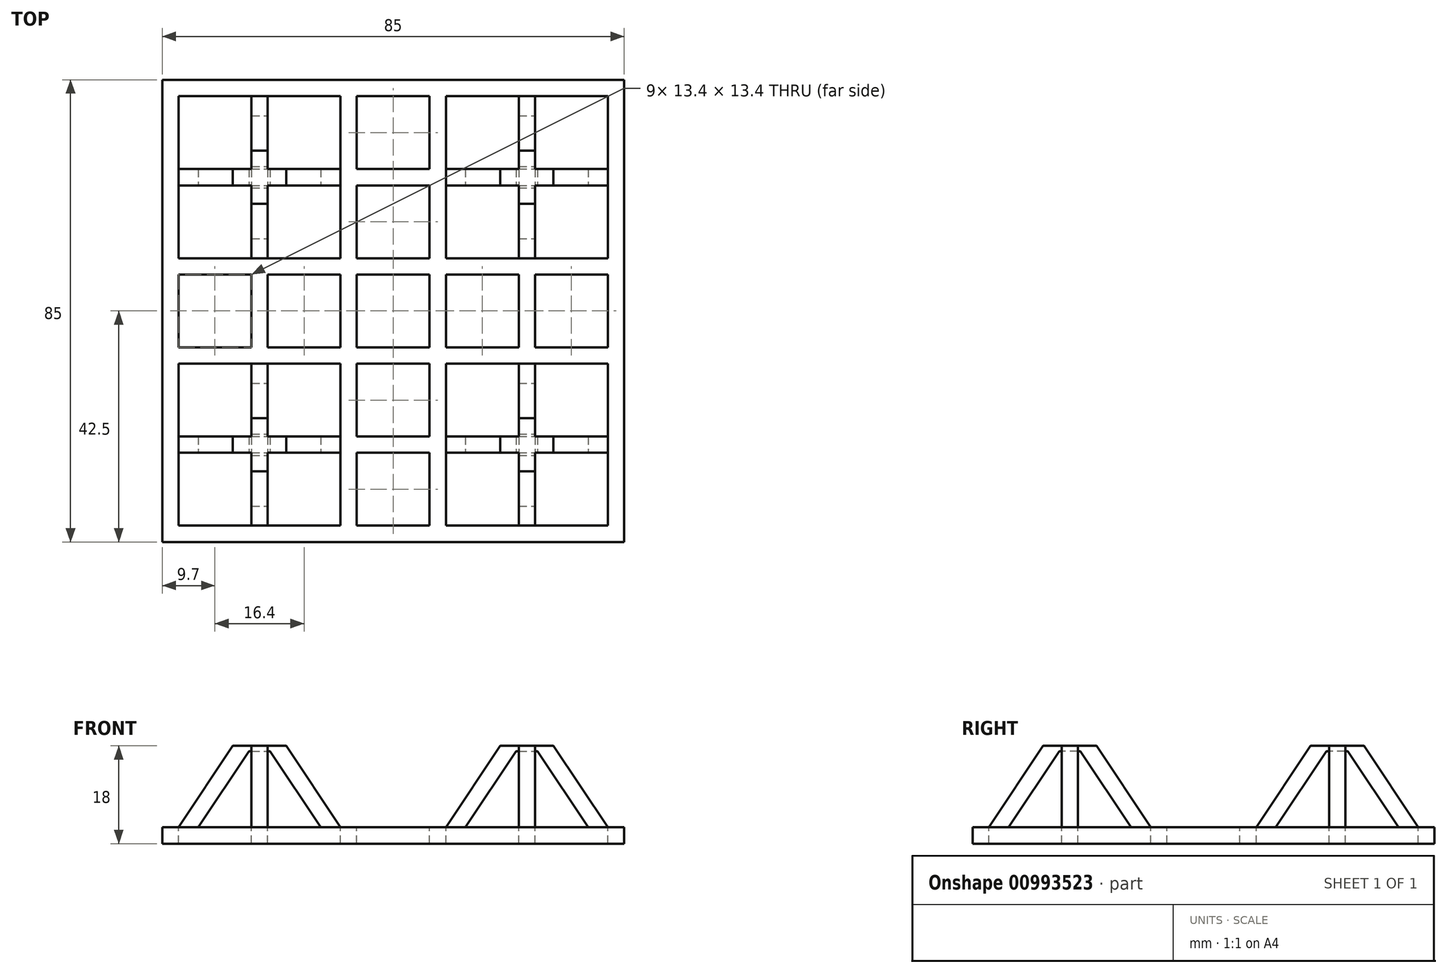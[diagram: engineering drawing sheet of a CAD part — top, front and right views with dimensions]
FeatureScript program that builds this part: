
annotation { "Feature Type Name" : "Feature", "Feature Type Description" : "" }
export const myFeature = defineFeature(function(context is Context, id is Id, definition is map)
    precondition{}
    {
        {
            var Q0;
            Q0=qCreatedBy(makeId("Top.planeOp"),FACE);
            var sketch = newSketch(context, id + "F0", { "sketchPlane" : qUnion([Q0])});
            skLineSegment(sketch, "E0.bottom", {"start": v(42.5, -42.5) * mm, "end": v(-42.5, -42.5) * mm});
            skLineSegment(sketch, "E0.top", {"start": v(42.5, 42.5) * mm, "end": v(-42.5, 42.5) * mm});
            skLineSegment(sketch, "E0.left", {"start": v(42.5, -42.5) * mm, "end": v(42.5, 42.5) * mm});
            skLineSegment(sketch, "E0.right", {"start": v(-42.5, -42.5) * mm, "end": v(-42.5, 42.5) * mm});
            skPoint(sketch, "E0.middle", {"position": v(0, 0) * mm});
            skSolve(sketch);
        }
        {
            var Q0;
            Q0=makeQuery(id+"F0.imprint","IMPRINT",FACE,{"disambiguationData":[TD([[makeQuery(id+"F0.imprint","IMPRINT",EDGE,{"derivedFrom":sQuery(id+"F0.wireOp",EDGE,"E0.bottom")}),-1.0]])]});
            extrude(context, id + "F1", {"entities" : qUnion([Q0]), "depth" : 3 * mm, "offsetDistance" : 25 * mm});
        }
        {
            var Q0;
            Q0=makeQuery(id+"F1.opExtrude","CAP_FACE",FACE,{"disambiguationData":[OSD([sQuery(id+"F0.wireOp",EDGE,"E0.bottom"),sQuery(id+"F0.wireOp",EDGE,"E0.top"),sQuery(id+"F0.wireOp",EDGE,"E0.left"),sQuery(id+"F0.wireOp",EDGE,"E0.right")])],"isStart":false});
            var sketch = newSketch(context, id + "F2", { "sketchPlane" : qUnion([Q0])});
            skLineSegment(sketch, "E1.bottom", {"start": v(-39.5, 39.5) * mm, "end": v(-26.1, 39.5) * mm});
            skLineSegment(sketch, "E1.top", {"start": v(-39.5, 26.1) * mm, "end": v(-26.1, 26.1) * mm});
            skLineSegment(sketch, "E1.left", {"start": v(-39.5, 39.5) * mm, "end": v(-39.5, 26.1) * mm});
            skLineSegment(sketch, "E1.right", {"start": v(-26.1, 39.5) * mm, "end": v(-26.1, 26.1) * mm});
            skLineSegment(sketch, "E2.0.1.0", {"start": v(-39.5, 23.1) * mm, "end": v(-26.1, 23.1) * mm});
            skLineSegment(sketch, "E2.0.1.1", {"start": v(-26.1, 23.1) * mm, "end": v(-26.1, 9.7) * mm});
            skLineSegment(sketch, "E2.0.1.2", {"start": v(-39.5, 9.7) * mm, "end": v(-26.1, 9.7) * mm});
            skLineSegment(sketch, "E2.0.1.3", {"start": v(-39.5, 23.1) * mm, "end": v(-39.5, 9.7) * mm});
            skLineSegment(sketch, "E2.0.2.0", {"start": v(-39.5, 6.7) * mm, "end": v(-26.1, 6.7) * mm});
            skLineSegment(sketch, "E2.0.2.1", {"start": v(-26.1, 6.7) * mm, "end": v(-26.1, -6.7) * mm});
            skLineSegment(sketch, "E2.0.2.2", {"start": v(-39.5, -6.7) * mm, "end": v(-26.1, -6.7) * mm});
            skLineSegment(sketch, "E2.0.2.3", {"start": v(-39.5, 6.7) * mm, "end": v(-39.5, -6.7) * mm});
            skLineSegment(sketch, "E2.0.3.0", {"start": v(-39.5, -9.7) * mm, "end": v(-26.1, -9.7) * mm});
            skLineSegment(sketch, "E2.0.3.1", {"start": v(-26.1, -9.7) * mm, "end": v(-26.1, -23.1) * mm});
            skLineSegment(sketch, "E2.0.3.2", {"start": v(-39.5, -23.1) * mm, "end": v(-26.1, -23.1) * mm});
            skLineSegment(sketch, "E2.0.3.3", {"start": v(-39.5, -9.7) * mm, "end": v(-39.5, -23.1) * mm});
            skLineSegment(sketch, "E2.0.4.0", {"start": v(-39.5, -26.1) * mm, "end": v(-26.1, -26.1) * mm});
            skLineSegment(sketch, "E2.0.4.1", {"start": v(-26.1, -26.1) * mm, "end": v(-26.1, -39.5) * mm});
            skLineSegment(sketch, "E2.0.4.2", {"start": v(-39.5, -39.5) * mm, "end": v(-26.1, -39.5) * mm});
            skLineSegment(sketch, "E2.0.4.3", {"start": v(-39.5, -26.1) * mm, "end": v(-39.5, -39.5) * mm});
            skLineSegment(sketch, "E2.1.0.0", {"start": v(-23.1, 39.5) * mm, "end": v(-9.7, 39.5) * mm});
            skLineSegment(sketch, "E2.1.0.1", {"start": v(-9.7, 39.5) * mm, "end": v(-9.7, 26.1) * mm});
            skLineSegment(sketch, "E2.1.0.2", {"start": v(-23.1, 26.1) * mm, "end": v(-9.7, 26.1) * mm});
            skLineSegment(sketch, "E2.1.0.3", {"start": v(-23.1, 39.5) * mm, "end": v(-23.1, 26.1) * mm});
            skLineSegment(sketch, "E2.1.1.0", {"start": v(-23.1, 23.1) * mm, "end": v(-9.7, 23.1) * mm});
            skLineSegment(sketch, "E2.1.1.1", {"start": v(-9.7, 23.1) * mm, "end": v(-9.7, 9.7) * mm});
            skLineSegment(sketch, "E2.1.1.2", {"start": v(-23.1, 9.7) * mm, "end": v(-9.7, 9.7) * mm});
            skLineSegment(sketch, "E2.1.1.3", {"start": v(-23.1, 23.1) * mm, "end": v(-23.1, 9.7) * mm});
            skLineSegment(sketch, "E2.1.2.0", {"start": v(-23.1, 6.7) * mm, "end": v(-9.7, 6.7) * mm});
            skLineSegment(sketch, "E2.1.2.1", {"start": v(-9.7, 6.7) * mm, "end": v(-9.7, -6.7) * mm});
            skLineSegment(sketch, "E2.1.2.2", {"start": v(-23.1, -6.7) * mm, "end": v(-9.7, -6.7) * mm});
            skLineSegment(sketch, "E2.1.2.3", {"start": v(-23.1, 6.7) * mm, "end": v(-23.1, -6.7) * mm});
            skLineSegment(sketch, "E2.1.3.0", {"start": v(-23.1, -9.7) * mm, "end": v(-9.7, -9.7) * mm});
            skLineSegment(sketch, "E2.1.3.1", {"start": v(-9.7, -9.7) * mm, "end": v(-9.7, -23.1) * mm});
            skLineSegment(sketch, "E2.1.3.2", {"start": v(-23.1, -23.1) * mm, "end": v(-9.7, -23.1) * mm});
            skLineSegment(sketch, "E2.1.3.3", {"start": v(-23.1, -9.7) * mm, "end": v(-23.1, -23.1) * mm});
            skLineSegment(sketch, "E2.1.4.0", {"start": v(-23.1, -26.1) * mm, "end": v(-9.7, -26.1) * mm});
            skLineSegment(sketch, "E2.1.4.1", {"start": v(-9.7, -26.1) * mm, "end": v(-9.7, -39.5) * mm});
            skLineSegment(sketch, "E2.1.4.2", {"start": v(-23.1, -39.5) * mm, "end": v(-9.7, -39.5) * mm});
            skLineSegment(sketch, "E2.1.4.3", {"start": v(-23.1, -26.1) * mm, "end": v(-23.1, -39.5) * mm});
            skLineSegment(sketch, "E2.2.0.0", {"start": v(-6.7, 39.5) * mm, "end": v(6.7, 39.5) * mm});
            skLineSegment(sketch, "E2.2.0.1", {"start": v(6.7, 39.5) * mm, "end": v(6.7, 26.1) * mm});
            skLineSegment(sketch, "E2.2.0.2", {"start": v(-6.7, 26.1) * mm, "end": v(6.7, 26.1) * mm});
            skLineSegment(sketch, "E2.2.0.3", {"start": v(-6.7, 39.5) * mm, "end": v(-6.7, 26.1) * mm});
            skLineSegment(sketch, "E2.2.1.0", {"start": v(-6.7, 23.1) * mm, "end": v(6.7, 23.1) * mm});
            skLineSegment(sketch, "E2.2.1.1", {"start": v(6.7, 23.1) * mm, "end": v(6.7, 9.7) * mm});
            skLineSegment(sketch, "E2.2.1.2", {"start": v(-6.7, 9.7) * mm, "end": v(6.7, 9.7) * mm});
            skLineSegment(sketch, "E2.2.1.3", {"start": v(-6.7, 23.1) * mm, "end": v(-6.7, 9.7) * mm});
            skLineSegment(sketch, "E2.2.2.0", {"start": v(-6.7, 6.7) * mm, "end": v(6.7, 6.7) * mm});
            skLineSegment(sketch, "E2.2.2.1", {"start": v(6.7, 6.7) * mm, "end": v(6.7, -6.7) * mm});
            skLineSegment(sketch, "E2.2.2.2", {"start": v(-6.7, -6.7) * mm, "end": v(6.7, -6.7) * mm});
            skLineSegment(sketch, "E2.2.2.3", {"start": v(-6.7, 6.7) * mm, "end": v(-6.7, -6.7) * mm});
            skLineSegment(sketch, "E2.2.3.0", {"start": v(-6.7, -9.7) * mm, "end": v(6.7, -9.7) * mm});
            skLineSegment(sketch, "E2.2.3.1", {"start": v(6.7, -9.7) * mm, "end": v(6.7, -23.1) * mm});
            skLineSegment(sketch, "E2.2.3.2", {"start": v(-6.7, -23.1) * mm, "end": v(6.7, -23.1) * mm});
            skLineSegment(sketch, "E2.2.3.3", {"start": v(-6.7, -9.7) * mm, "end": v(-6.7, -23.1) * mm});
            skLineSegment(sketch, "E2.2.4.0", {"start": v(-6.7, -26.1) * mm, "end": v(6.7, -26.1) * mm});
            skLineSegment(sketch, "E2.2.4.1", {"start": v(6.7, -26.1) * mm, "end": v(6.7, -39.5) * mm});
            skLineSegment(sketch, "E2.2.4.2", {"start": v(-6.7, -39.5) * mm, "end": v(6.7, -39.5) * mm});
            skLineSegment(sketch, "E2.2.4.3", {"start": v(-6.7, -26.1) * mm, "end": v(-6.7, -39.5) * mm});
            skLineSegment(sketch, "E2.3.0.0", {"start": v(9.7, 39.5) * mm, "end": v(23.1, 39.5) * mm});
            skLineSegment(sketch, "E2.3.0.1", {"start": v(23.1, 39.5) * mm, "end": v(23.1, 26.1) * mm});
            skLineSegment(sketch, "E2.3.0.2", {"start": v(9.7, 26.1) * mm, "end": v(23.1, 26.1) * mm});
            skLineSegment(sketch, "E2.3.0.3", {"start": v(9.7, 39.5) * mm, "end": v(9.7, 26.1) * mm});
            skLineSegment(sketch, "E2.3.1.0", {"start": v(9.7, 23.1) * mm, "end": v(23.1, 23.1) * mm});
            skLineSegment(sketch, "E2.3.1.1", {"start": v(23.1, 23.1) * mm, "end": v(23.1, 9.7) * mm});
            skLineSegment(sketch, "E2.3.1.2", {"start": v(9.7, 9.7) * mm, "end": v(23.1, 9.7) * mm});
            skLineSegment(sketch, "E2.3.1.3", {"start": v(9.7, 23.1) * mm, "end": v(9.7, 9.7) * mm});
            skLineSegment(sketch, "E2.3.2.0", {"start": v(9.7, 6.7) * mm, "end": v(23.1, 6.7) * mm});
            skLineSegment(sketch, "E2.3.2.1", {"start": v(23.1, 6.7) * mm, "end": v(23.1, -6.7) * mm});
            skLineSegment(sketch, "E2.3.2.2", {"start": v(9.7, -6.7) * mm, "end": v(23.1, -6.7) * mm});
            skLineSegment(sketch, "E2.3.2.3", {"start": v(9.7, 6.7) * mm, "end": v(9.7, -6.7) * mm});
            skLineSegment(sketch, "E2.3.3.0", {"start": v(9.7, -9.7) * mm, "end": v(23.1, -9.7) * mm});
            skLineSegment(sketch, "E2.3.3.1", {"start": v(23.1, -9.7) * mm, "end": v(23.1, -23.1) * mm});
            skLineSegment(sketch, "E2.3.3.2", {"start": v(9.7, -23.1) * mm, "end": v(23.1, -23.1) * mm});
            skLineSegment(sketch, "E2.3.3.3", {"start": v(9.7, -9.7) * mm, "end": v(9.7, -23.1) * mm});
            skLineSegment(sketch, "E2.3.4.0", {"start": v(9.7, -26.1) * mm, "end": v(23.1, -26.1) * mm});
            skLineSegment(sketch, "E2.3.4.1", {"start": v(23.1, -26.1) * mm, "end": v(23.1, -39.5) * mm});
            skLineSegment(sketch, "E2.3.4.2", {"start": v(9.7, -39.5) * mm, "end": v(23.1, -39.5) * mm});
            skLineSegment(sketch, "E2.3.4.3", {"start": v(9.7, -26.1) * mm, "end": v(9.7, -39.5) * mm});
            skLineSegment(sketch, "E2.4.0.0", {"start": v(26.1, 39.5) * mm, "end": v(39.5, 39.5) * mm});
            skLineSegment(sketch, "E2.4.0.1", {"start": v(39.5, 39.5) * mm, "end": v(39.5, 26.1) * mm});
            skLineSegment(sketch, "E2.4.0.2", {"start": v(26.1, 26.1) * mm, "end": v(39.5, 26.1) * mm});
            skLineSegment(sketch, "E2.4.0.3", {"start": v(26.1, 39.5) * mm, "end": v(26.1, 26.1) * mm});
            skLineSegment(sketch, "E2.4.1.0", {"start": v(26.1, 23.1) * mm, "end": v(39.5, 23.1) * mm});
            skLineSegment(sketch, "E2.4.1.1", {"start": v(39.5, 23.1) * mm, "end": v(39.5, 9.7) * mm});
            skLineSegment(sketch, "E2.4.1.2", {"start": v(26.1, 9.7) * mm, "end": v(39.5, 9.7) * mm});
            skLineSegment(sketch, "E2.4.1.3", {"start": v(26.1, 23.1) * mm, "end": v(26.1, 9.7) * mm});
            skLineSegment(sketch, "E2.4.2.0", {"start": v(26.1, 6.7) * mm, "end": v(39.5, 6.7) * mm});
            skLineSegment(sketch, "E2.4.2.1", {"start": v(39.5, 6.7) * mm, "end": v(39.5, -6.7) * mm});
            skLineSegment(sketch, "E2.4.2.2", {"start": v(26.1, -6.7) * mm, "end": v(39.5, -6.7) * mm});
            skLineSegment(sketch, "E2.4.2.3", {"start": v(26.1, 6.7) * mm, "end": v(26.1, -6.7) * mm});
            skLineSegment(sketch, "E2.4.3.0", {"start": v(26.1, -9.7) * mm, "end": v(39.5, -9.7) * mm});
            skLineSegment(sketch, "E2.4.3.1", {"start": v(39.5, -9.7) * mm, "end": v(39.5, -23.1) * mm});
            skLineSegment(sketch, "E2.4.3.2", {"start": v(26.1, -23.1) * mm, "end": v(39.5, -23.1) * mm});
            skLineSegment(sketch, "E2.4.3.3", {"start": v(26.1, -9.7) * mm, "end": v(26.1, -23.1) * mm});
            skLineSegment(sketch, "E2.4.4.0", {"start": v(26.1, -26.1) * mm, "end": v(39.5, -26.1) * mm});
            skLineSegment(sketch, "E2.4.4.1", {"start": v(39.5, -26.1) * mm, "end": v(39.5, -39.5) * mm});
            skLineSegment(sketch, "E2.4.4.2", {"start": v(26.1, -39.5) * mm, "end": v(39.5, -39.5) * mm});
            skLineSegment(sketch, "E2.4.4.3", {"start": v(26.1, -26.1) * mm, "end": v(26.1, -39.5) * mm});
            skLineSegment(sketch, "E2.direction1", {"start": v(-39.5, 39.5) * mm, "end": v(-23.1, 39.5) * mm, "construction": true});
            skLineSegment(sketch, "E2.direction2", {"start": v(-39.5, 39.5) * mm, "end": v(-39.5, 23.1) * mm, "construction": true});
            skSolve(sketch);
        }
        {
            var Q0;
            Q0=makeQuery(id+"F2.imprint","IMPRINT",FACE,{"disambiguationData":[TD([[makeQuery(id+"F2.imprint","IMPRINT",EDGE,{"derivedFrom":sQuery(id+"F2.wireOp",EDGE,"E2.0.1.0")}),-1.0]])]});
            var Q1;
            Q1=makeQuery(id+"F2.imprint","IMPRINT",FACE,{"disambiguationData":[TD([[makeQuery(id+"F2.imprint","IMPRINT",EDGE,{"derivedFrom":sQuery(id+"F2.wireOp",EDGE,"E2.0.2.0")}),-1.0]])]});
            var Q2;
            Q2=makeQuery(id+"F2.imprint","IMPRINT",FACE,{"disambiguationData":[TD([[makeQuery(id+"F2.imprint","IMPRINT",EDGE,{"derivedFrom":sQuery(id+"F2.wireOp",EDGE,"E2.0.3.0")}),-1.0]])]});
            var Q3;
            Q3=makeQuery(id+"F2.imprint","IMPRINT",FACE,{"disambiguationData":[TD([[makeQuery(id+"F2.imprint","IMPRINT",EDGE,{"derivedFrom":sQuery(id+"F2.wireOp",EDGE,"E2.0.4.0")}),-1.0]])]});
            var Q4;
            Q4=makeQuery(id+"F2.imprint","IMPRINT",FACE,{"disambiguationData":[TD([[makeQuery(id+"F2.imprint","IMPRINT",EDGE,{"derivedFrom":sQuery(id+"F2.wireOp",EDGE,"E2.0.5.0")}),-1.0]])]});
            var Q5;
            Q5=makeQuery(id+"F2.imprint","IMPRINT",FACE,{"disambiguationData":[TD([[makeQuery(id+"F2.imprint","IMPRINT",EDGE,{"derivedFrom":sQuery(id+"F2.wireOp",EDGE,"E2.0.6.0")}),-1.0]])]});
            var Q6;
            Q6=makeQuery(id+"F2.imprint","IMPRINT",FACE,{"disambiguationData":[TD([[makeQuery(id+"F2.imprint","IMPRINT",EDGE,{"derivedFrom":sQuery(id+"F2.wireOp",EDGE,"E2.1.0.0")}),-1.0]])]});
            var Q7;
            Q7=makeQuery(id+"F2.imprint","IMPRINT",FACE,{"disambiguationData":[TD([[makeQuery(id+"F2.imprint","IMPRINT",EDGE,{"derivedFrom":sQuery(id+"F2.wireOp",EDGE,"E2.1.1.0")}),-1.0]])]});
            var Q8;
            Q8=makeQuery(id+"F2.imprint","IMPRINT",FACE,{"disambiguationData":[TD([[makeQuery(id+"F2.imprint","IMPRINT",EDGE,{"derivedFrom":sQuery(id+"F2.wireOp",EDGE,"E2.1.2.0")}),-1.0]])]});
            var Q9;
            Q9=makeQuery(id+"F2.imprint","IMPRINT",FACE,{"disambiguationData":[TD([[makeQuery(id+"F2.imprint","IMPRINT",EDGE,{"derivedFrom":sQuery(id+"F2.wireOp",EDGE,"E2.1.3.0")}),-1.0]])]});
            var Q10;
            Q10=makeQuery(id+"F2.imprint","IMPRINT",FACE,{"disambiguationData":[TD([[makeQuery(id+"F2.imprint","IMPRINT",EDGE,{"derivedFrom":sQuery(id+"F2.wireOp",EDGE,"E2.1.4.0")}),-1.0]])]});
            var Q11;
            Q11=makeQuery(id+"F2.imprint","IMPRINT",FACE,{"disambiguationData":[TD([[makeQuery(id+"F2.imprint","IMPRINT",EDGE,{"derivedFrom":sQuery(id+"F2.wireOp",EDGE,"E2.1.5.0")}),-1.0]])]});
            var Q12;
            Q12=makeQuery(id+"F2.imprint","IMPRINT",FACE,{"disambiguationData":[TD([[makeQuery(id+"F2.imprint","IMPRINT",EDGE,{"derivedFrom":sQuery(id+"F2.wireOp",EDGE,"E2.1.6.0")}),-1.0]])]});
            var Q13;
            Q13=makeQuery(id+"F2.imprint","IMPRINT",FACE,{"disambiguationData":[TD([[makeQuery(id+"F2.imprint","IMPRINT",EDGE,{"derivedFrom":sQuery(id+"F2.wireOp",EDGE,"E2.2.0.0")}),-1.0]])]});
            var Q14;
            Q14=makeQuery(id+"F2.imprint","IMPRINT",FACE,{"disambiguationData":[TD([[makeQuery(id+"F2.imprint","IMPRINT",EDGE,{"derivedFrom":sQuery(id+"F2.wireOp",EDGE,"E2.2.1.0")}),-1.0]])]});
            var Q15;
            Q15=makeQuery(id+"F2.imprint","IMPRINT",FACE,{"disambiguationData":[TD([[makeQuery(id+"F2.imprint","IMPRINT",EDGE,{"derivedFrom":sQuery(id+"F2.wireOp",EDGE,"E2.2.2.0")}),-1.0]])]});
            var Q16;
            Q16=makeQuery(id+"F2.imprint","IMPRINT",FACE,{"disambiguationData":[TD([[makeQuery(id+"F2.imprint","IMPRINT",EDGE,{"derivedFrom":sQuery(id+"F2.wireOp",EDGE,"E2.2.3.0")}),-1.0]])]});
            var Q17;
            Q17=makeQuery(id+"F2.imprint","IMPRINT",FACE,{"disambiguationData":[TD([[makeQuery(id+"F2.imprint","IMPRINT",EDGE,{"derivedFrom":sQuery(id+"F2.wireOp",EDGE,"E2.2.4.0")}),-1.0]])]});
            var Q18;
            Q18=makeQuery(id+"F2.imprint","IMPRINT",FACE,{"disambiguationData":[TD([[makeQuery(id+"F2.imprint","IMPRINT",EDGE,{"derivedFrom":sQuery(id+"F2.wireOp",EDGE,"E2.2.5.0")}),-1.0]])]});
            var Q19;
            Q19=makeQuery(id+"F2.imprint","IMPRINT",FACE,{"disambiguationData":[TD([[makeQuery(id+"F2.imprint","IMPRINT",EDGE,{"derivedFrom":sQuery(id+"F2.wireOp",EDGE,"E2.2.6.0")}),-1.0]])]});
            var Q20;
            Q20=makeQuery(id+"F2.imprint","IMPRINT",FACE,{"disambiguationData":[TD([[makeQuery(id+"F2.imprint","IMPRINT",EDGE,{"derivedFrom":sQuery(id+"F2.wireOp",EDGE,"E2.3.0.0")}),-1.0]])]});
            var Q21;
            Q21=makeQuery(id+"F2.imprint","IMPRINT",FACE,{"disambiguationData":[TD([[makeQuery(id+"F2.imprint","IMPRINT",EDGE,{"derivedFrom":sQuery(id+"F2.wireOp",EDGE,"E2.3.1.0")}),-1.0]])]});
            var Q22;
            Q22=makeQuery(id+"F2.imprint","IMPRINT",FACE,{"disambiguationData":[TD([[makeQuery(id+"F2.imprint","IMPRINT",EDGE,{"derivedFrom":sQuery(id+"F2.wireOp",EDGE,"E2.3.2.0")}),-1.0]])]});
            var Q23;
            Q23=makeQuery(id+"F2.imprint","IMPRINT",FACE,{"disambiguationData":[TD([[makeQuery(id+"F2.imprint","IMPRINT",EDGE,{"derivedFrom":sQuery(id+"F2.wireOp",EDGE,"E2.3.3.0")}),-1.0]])]});
            var Q24;
            Q24=makeQuery(id+"F2.imprint","IMPRINT",FACE,{"disambiguationData":[TD([[makeQuery(id+"F2.imprint","IMPRINT",EDGE,{"derivedFrom":sQuery(id+"F2.wireOp",EDGE,"E2.3.4.0")}),-1.0]])]});
            var Q25;
            Q25=makeQuery(id+"F2.imprint","IMPRINT",FACE,{"disambiguationData":[TD([[makeQuery(id+"F2.imprint","IMPRINT",EDGE,{"derivedFrom":sQuery(id+"F2.wireOp",EDGE,"E2.3.5.0")}),-1.0]])]});
            var Q26;
            Q26=makeQuery(id+"F2.imprint","IMPRINT",FACE,{"disambiguationData":[TD([[makeQuery(id+"F2.imprint","IMPRINT",EDGE,{"derivedFrom":sQuery(id+"F2.wireOp",EDGE,"E2.3.6.0")}),-1.0]])]});
            var Q27;
            Q27=makeQuery(id+"F2.imprint","IMPRINT",FACE,{"disambiguationData":[TD([[makeQuery(id+"F2.imprint","IMPRINT",EDGE,{"derivedFrom":sQuery(id+"F2.wireOp",EDGE,"E2.4.0.0")}),-1.0]])]});
            var Q28;
            Q28=makeQuery(id+"F2.imprint","IMPRINT",FACE,{"disambiguationData":[TD([[makeQuery(id+"F2.imprint","IMPRINT",EDGE,{"derivedFrom":sQuery(id+"F2.wireOp",EDGE,"E2.4.1.0")}),-1.0]])]});
            var Q29;
            Q29=makeQuery(id+"F2.imprint","IMPRINT",FACE,{"disambiguationData":[TD([[makeQuery(id+"F2.imprint","IMPRINT",EDGE,{"derivedFrom":sQuery(id+"F2.wireOp",EDGE,"E2.4.2.0")}),-1.0]])]});
            var Q30;
            Q30=makeQuery(id+"F2.imprint","IMPRINT",FACE,{"disambiguationData":[TD([[makeQuery(id+"F2.imprint","IMPRINT",EDGE,{"derivedFrom":sQuery(id+"F2.wireOp",EDGE,"E2.4.3.0")}),-1.0]])]});
            var Q31;
            Q31=makeQuery(id+"F2.imprint","IMPRINT",FACE,{"disambiguationData":[TD([[makeQuery(id+"F2.imprint","IMPRINT",EDGE,{"derivedFrom":sQuery(id+"F2.wireOp",EDGE,"E2.4.4.0")}),-1.0]])]});
            var Q32;
            Q32=makeQuery(id+"F2.imprint","IMPRINT",FACE,{"disambiguationData":[TD([[makeQuery(id+"F2.imprint","IMPRINT",EDGE,{"derivedFrom":sQuery(id+"F2.wireOp",EDGE,"E2.4.5.0")}),-1.0]])]});
            var Q33;
            Q33=makeQuery(id+"F2.imprint","IMPRINT",FACE,{"disambiguationData":[TD([[makeQuery(id+"F2.imprint","IMPRINT",EDGE,{"derivedFrom":sQuery(id+"F2.wireOp",EDGE,"E2.4.6.0")}),-1.0]])]});
            var Q34;
            Q34=makeQuery(id+"F2.imprint","IMPRINT",FACE,{"disambiguationData":[TD([[makeQuery(id+"F2.imprint","IMPRINT",EDGE,{"derivedFrom":sQuery(id+"F2.wireOp",EDGE,"E2.5.0.0")}),-1.0]])]});
            var Q35;
            Q35=makeQuery(id+"F2.imprint","IMPRINT",FACE,{"disambiguationData":[TD([[makeQuery(id+"F2.imprint","IMPRINT",EDGE,{"derivedFrom":sQuery(id+"F2.wireOp",EDGE,"E2.5.1.0")}),-1.0]])]});
            var Q36;
            Q36=makeQuery(id+"F2.imprint","IMPRINT",FACE,{"disambiguationData":[TD([[makeQuery(id+"F2.imprint","IMPRINT",EDGE,{"derivedFrom":sQuery(id+"F2.wireOp",EDGE,"E2.5.2.0")}),-1.0]])]});
            var Q37;
            Q37=makeQuery(id+"F2.imprint","IMPRINT",FACE,{"disambiguationData":[TD([[makeQuery(id+"F2.imprint","IMPRINT",EDGE,{"derivedFrom":sQuery(id+"F2.wireOp",EDGE,"E2.5.3.0")}),-1.0]])]});
            var Q38;
            Q38=makeQuery(id+"F2.imprint","IMPRINT",FACE,{"disambiguationData":[TD([[makeQuery(id+"F2.imprint","IMPRINT",EDGE,{"derivedFrom":sQuery(id+"F2.wireOp",EDGE,"E2.5.4.0")}),-1.0]])]});
            var Q39;
            Q39=makeQuery(id+"F2.imprint","IMPRINT",FACE,{"disambiguationData":[TD([[makeQuery(id+"F2.imprint","IMPRINT",EDGE,{"derivedFrom":sQuery(id+"F2.wireOp",EDGE,"E2.5.5.0")}),-1.0]])]});
            var Q40;
            Q40=makeQuery(id+"F2.imprint","IMPRINT",FACE,{"disambiguationData":[TD([[makeQuery(id+"F2.imprint","IMPRINT",EDGE,{"derivedFrom":sQuery(id+"F2.wireOp",EDGE,"E2.5.6.0")}),-1.0]])]});
            var Q41;
            Q41=makeQuery(id+"F2.imprint","IMPRINT",FACE,{"disambiguationData":[TD([[makeQuery(id+"F2.imprint","IMPRINT",EDGE,{"derivedFrom":sQuery(id+"F2.wireOp",EDGE,"E2.6.0.0")}),-1.0]])]});
            var Q42;
            Q42=makeQuery(id+"F2.imprint","IMPRINT",FACE,{"disambiguationData":[TD([[makeQuery(id+"F2.imprint","IMPRINT",EDGE,{"derivedFrom":sQuery(id+"F2.wireOp",EDGE,"E2.6.1.0")}),-1.0]])]});
            var Q43;
            Q43=makeQuery(id+"F2.imprint","IMPRINT",FACE,{"disambiguationData":[TD([[makeQuery(id+"F2.imprint","IMPRINT",EDGE,{"derivedFrom":sQuery(id+"F2.wireOp",EDGE,"E2.6.2.0")}),-1.0]])]});
            var Q44;
            Q44=makeQuery(id+"F2.imprint","IMPRINT",FACE,{"disambiguationData":[TD([[makeQuery(id+"F2.imprint","IMPRINT",EDGE,{"derivedFrom":sQuery(id+"F2.wireOp",EDGE,"E2.6.3.0")}),-1.0]])]});
            var Q45;
            Q45=makeQuery(id+"F2.imprint","IMPRINT",FACE,{"disambiguationData":[TD([[makeQuery(id+"F2.imprint","IMPRINT",EDGE,{"derivedFrom":sQuery(id+"F2.wireOp",EDGE,"E2.6.4.0")}),-1.0]])]});
            var Q46;
            Q46=makeQuery(id+"F2.imprint","IMPRINT",FACE,{"disambiguationData":[TD([[makeQuery(id+"F2.imprint","IMPRINT",EDGE,{"derivedFrom":sQuery(id+"F2.wireOp",EDGE,"E2.6.5.0")}),-1.0]])]});
            var Q47;
            Q47=makeQuery(id+"F2.imprint","IMPRINT",FACE,{"disambiguationData":[TD([[makeQuery(id+"F2.imprint","IMPRINT",EDGE,{"derivedFrom":sQuery(id+"F2.wireOp",EDGE,"E2.6.6.0")}),-1.0]])]});
            var Q48;
            Q48=makeQuery(id+"F2.imprint","IMPRINT",FACE,{"disambiguationData":[TD([[makeQuery(id+"F2.imprint","IMPRINT",EDGE,{"derivedFrom":sQuery(id+"F2.wireOp",EDGE,"E1.bottom")}),-1.0]])]});
            extrude(context, id + "F3", {"entities" : qUnion([Q0, Q1, Q2, Q3, Q4, Q5, Q6, Q7, Q8, Q9, Q10, Q11, Q12, Q13, Q14, Q15, Q16, Q17, Q18, Q19, Q20, Q21, Q22, Q23, Q24, Q25, Q26, Q27, Q28, Q29, Q30, Q31, Q32, Q33, Q34, Q35, Q36, Q37, Q38, Q39, Q40, Q41, Q42, Q43, Q44, Q45, Q46, Q47, Q48]), "operationType" : NewBodyOperationType.REMOVE, "oppositeDirection" : true, "depth" : 25 * mm, "offsetDistance" : 25 * mm});
        }
        {
            var Q0;
            Q0=makeQuery(id+"F1.opExtrude","CAP_FACE",FACE,{"disambiguationData":[OSD([sQuery(id+"F0.wireOp",EDGE,"E0.bottom"),sQuery(id+"F0.wireOp",EDGE,"E0.top"),sQuery(id+"F0.wireOp",EDGE,"E0.left"),sQuery(id+"F0.wireOp",EDGE,"E0.right")])],"isStart":false});
            var sketch = newSketch(context, id + "F4", { "sketchPlane" : qUnion([Q0])});
            skLineSegment(sketch, "E3", {"start": v(-26.1, -9.7) * mm, "end": v(-23.1, -9.7) * mm});
            skLineSegment(sketch, "E4", {"start": v(-9.7, -23.1) * mm, "end": v(-9.7, -26.1) * mm});
            skLineSegment(sketch, "E5", {"start": v(-23.1, -39.5) * mm, "end": v(-26.1, -39.5) * mm});
            skLineSegment(sketch, "E6", {"start": v(-39.5, -23.1) * mm, "end": v(-39.5, -26.1) * mm});
            skLineSegment(sketch, "E7", {"start": v(-9.7, 26.1) * mm, "end": v(-9.7, 23.1) * mm});
            skLineSegment(sketch, "E8", {"start": v(-23.1, 9.7) * mm, "end": v(-26.1, 9.7) * mm});
            skLineSegment(sketch, "E9", {"start": v(-39.5, 26.1) * mm, "end": v(-39.5, 23.1) * mm});
            skLineSegment(sketch, "E10", {"start": v(-23.1, 39.5) * mm, "end": v(-26.1, 39.5) * mm});
            skLineSegment(sketch, "E11", {"start": v(26.1, 39.5) * mm, "end": v(23.1, 39.5) * mm});
            skLineSegment(sketch, "E12", {"start": v(39.5, 26.1) * mm, "end": v(39.5, 23.1) * mm});
            skLineSegment(sketch, "E13", {"start": v(26.1, 9.7) * mm, "end": v(23.1, 9.7) * mm});
            skLineSegment(sketch, "E14", {"start": v(9.7, 26.1) * mm, "end": v(9.7, 23.1) * mm});
            skLineSegment(sketch, "E15", {"start": v(26.1, -9.7) * mm, "end": v(23.1, -9.7) * mm});
            skLineSegment(sketch, "E16", {"start": v(39.5, -26.1) * mm, "end": v(39.5, -23.1) * mm});
            skLineSegment(sketch, "E17", {"start": v(26.1, -39.5) * mm, "end": v(23.1, -39.5) * mm});
            skLineSegment(sketch, "E18", {"start": v(9.7, -23.1) * mm, "end": v(9.7, -26.1) * mm});
            skSolve(sketch);
        }
        {
            var Q0;
            Q0 = qSketchRegion(id + "F4", true);
            var Q1;
            Q1=makeQuery(id+"F4.imprint","IMPRINT",FACE,{"disambiguationData":[TD([[makeQuery(id+"F4.imprint","IMPRINT",EDGE,{"derivedFrom":sQuery(id+"F4.wireOp",EDGE,"E3")}),-1.0]])]});
            var Q2;
            Q2=makeQuery(id+"F4.imprint","IMPRINT",FACE,{"disambiguationData":[TD([[makeQuery(id+"F4.imprint","IMPRINT",EDGE,{"derivedFrom":sQuery(id+"F4.wireOp",EDGE,"E7")}),-1.0]])]});
            var Q3;
            Q3=makeQuery(id+"F4.imprint","IMPRINT",FACE,{"disambiguationData":[TD([[makeQuery(id+"F4.imprint","IMPRINT",EDGE,{"derivedFrom":sQuery(id+"F4.wireOp",EDGE,"E11")}),1.0]])]});
            var Q4;
            Q4=makeQuery(id+"F4.imprint","IMPRINT",FACE,{"disambiguationData":[TD([[makeQuery(id+"F4.imprint","IMPRINT",EDGE,{"derivedFrom":sQuery(id+"F4.wireOp",EDGE,"E15")}),1.0]])]});
            extrude(context, id + "F5", {"entities" : qUnion([Q0, Q1, Q2, Q3, Q4]), "operationType" : NewBodyOperationType.ADD, "depth" : 15 * mm, "offsetDistance" : 25 * mm});
        }
        {
            var Q0;
            Q0=makeQuery(id+"F5.opExtrude","CAP_EDGE",EDGE,{"disambiguationData":[OSD([sQuery(id+"F4.wireOp",EDGE,"E6")])],"isStart":false});
            var Q1;
            Q1=makeQuery(id+"F5.opExtrude","CAP_EDGE",EDGE,{"disambiguationData":[OSD([sQuery(id+"F4.wireOp",EDGE,"E3")])],"isStart":false});
            var Q2;
            Q2=makeQuery(id+"F5.opExtrude","CAP_EDGE",EDGE,{"disambiguationData":[OSD([sQuery(id+"F4.wireOp",EDGE,"E4")])],"isStart":false});
            var Q3;
            Q3=makeQuery(id+"F5.opExtrude","CAP_EDGE",EDGE,{"disambiguationData":[OSD([sQuery(id+"F4.wireOp",EDGE,"E5")])],"isStart":false});
            var Q4;
            Q4=makeQuery(id+"F5.opExtrude","CAP_EDGE",EDGE,{"disambiguationData":[OSD([sQuery(id+"F4.wireOp",EDGE,"E9")])],"isStart":false});
            var Q5;
            Q5=makeQuery(id+"F5.opExtrude","CAP_EDGE",EDGE,{"disambiguationData":[OSD([sQuery(id+"F4.wireOp",EDGE,"E10")])],"isStart":false});
            var Q6;
            Q6=makeQuery(id+"F5.opExtrude","CAP_EDGE",EDGE,{"disambiguationData":[OSD([sQuery(id+"F4.wireOp",EDGE,"E14")])],"isStart":false});
            var Q7;
            Q7=makeQuery(id+"F5.opExtrude","CAP_EDGE",EDGE,{"disambiguationData":[OSD([sQuery(id+"F4.wireOp",EDGE,"E11")])],"isStart":false});
            var Q8;
            Q8=makeQuery(id+"F5.opExtrude","CAP_EDGE",EDGE,{"disambiguationData":[OSD([sQuery(id+"F4.wireOp",EDGE,"E15")])],"isStart":false});
            var Q9;
            Q9=makeQuery(id+"F5.opExtrude","CAP_EDGE",EDGE,{"disambiguationData":[OSD([sQuery(id+"F4.wireOp",EDGE,"E18")])],"isStart":false});
            var Q10;
            Q10=makeQuery(id+"F5.opExtrude","CAP_EDGE",EDGE,{"disambiguationData":[OSD([sQuery(id+"F4.wireOp",EDGE,"E16")])],"isStart":false});
            chamfer(context, id + "F6", {"entities" : qUnion([Q0, Q1, Q2, Q3, Q4, Q5, Q6, Q7, Q8, Q9, Q10]), "chamferType" : ChamferType.TWO_OFFSETS, "width1" : 10 * mm, "oppositeDirection" : false, "width2" : 15 * mm, "tangentPropagation" : true});
        }
        {
            var Q0;
            Q0=makeQuery(id+"F5.opExtrude","CAP_EDGE",EDGE,{"disambiguationData":[OSD([sQuery(id+"F4.wireOp",EDGE,"E7")])],"isStart":false});
            var Q1;
            Q1=makeQuery(id+"F5.opExtrude","CAP_EDGE",EDGE,{"disambiguationData":[OSD([sQuery(id+"F4.wireOp",EDGE,"E8")])],"isStart":false});
            var Q2;
            Q2=makeQuery(id+"F5.opExtrude","CAP_EDGE",EDGE,{"disambiguationData":[OSD([sQuery(id+"F4.wireOp",EDGE,"E13")])],"isStart":false});
            var Q3;
            Q3=makeQuery(id+"F5.opExtrude","CAP_EDGE",EDGE,{"disambiguationData":[OSD([sQuery(id+"F4.wireOp",EDGE,"E12")])],"isStart":false});
            var Q4;
            Q4=makeQuery(id+"F5.opExtrude","CAP_EDGE",EDGE,{"disambiguationData":[OSD([sQuery(id+"F4.wireOp",EDGE,"E17")])],"isStart":false});
            chamfer(context, id + "F7", {"entities" : qUnion([Q0, Q1, Q2, Q3, Q4]), "chamferType" : ChamferType.TWO_OFFSETS, "width1" : 15 * mm, "oppositeDirection" : false, "width2" : 10 * mm, "tangentPropagation" : true});
        }
        {
            var Q0;
            {var subQ0=sQuery(id+"F2.wireOp",EDGE,"E2.4.4.3");Q0=makeQuery(id+"F5.boolean.opBoolean","MERGE",FACE,{"derivedFrom":[makeQuery(id+"F3.boolean.opBoolean","COPY",FACE,{"derivedFrom":makeQuery(id+"F3.opExtrude","SWEPT_FACE",FACE,{"disambiguationData":[OSD([subQ0])]})}),makeQuery(id+"F5.opExtrude","SWEPT_FACE",FACE,{"disambiguationData":[OSD([subQ0])]})]});}
            var sketch = newSketch(context, id + "F8", { "sketchPlane" : qUnion([Q0])});
            skLineSegment(sketch, "E19", {"start": v(-26.56, 17) * mm, "end": v(-35.9, 3) * mm});
            skLineSegment(sketch, "E20", {"start": v(-35.9, 3) * mm, "end": v(-26.1, 3) * mm});
            skLineSegment(sketch, "E21", {"start": v(-26.1, 3) * mm, "end": v(-26.1, 17) * mm});
            skLineSegment(sketch, "E22", {"start": v(-26.1, 17) * mm, "end": v(-26.56, 17) * mm});
            skLineSegment(sketch, "E23", {"start": v(-23.1, 17) * mm, "end": v(-22.64, 17) * mm});
            skLineSegment(sketch, "E24", {"start": v(-22.64, 17) * mm, "end": v(-13.3, 3) * mm});
            skLineSegment(sketch, "E25", {"start": v(-13.3, 3) * mm, "end": v(-23.1, 3) * mm});
            skLineSegment(sketch, "E26", {"start": v(-23.1, 3) * mm, "end": v(-23.1, 17) * mm});
            skLineSegment(sketch, "E27", {"start": v(22.64, 17) * mm, "end": v(13.3, 3) * mm});
            skLineSegment(sketch, "E28", {"start": v(13.3, 3) * mm, "end": v(23.1, 3) * mm});
            skLineSegment(sketch, "E29", {"start": v(23.1, 3) * mm, "end": v(23.1, 17) * mm});
            skLineSegment(sketch, "E30", {"start": v(23.1, 17) * mm, "end": v(22.64, 17) * mm});
            skLineSegment(sketch, "E31", {"start": v(26.1, 17) * mm, "end": v(26.56, 17) * mm});
            skLineSegment(sketch, "E32", {"start": v(26.56, 17) * mm, "end": v(35.9, 3) * mm});
            skLineSegment(sketch, "E33", {"start": v(35.9, 3) * mm, "end": v(26.1, 3) * mm});
            skLineSegment(sketch, "E34", {"start": v(26.1, 3) * mm, "end": v(26.1, 17) * mm});
            skSolve(sketch);
        }
        {
            var Q0;
            Q0=makeQuery(id+"F8.imprint","IMPRINT",FACE,{"disambiguationData":[TD([[makeQuery(id+"F8.imprint","IMPRINT",EDGE,{"derivedFrom":sQuery(id+"F8.wireOp",EDGE,"E19")}),1.0]])]});
            var Q1;
            Q1=makeQuery(id+"F8.imprint","IMPRINT",FACE,{"disambiguationData":[TD([[makeQuery(id+"F8.imprint","IMPRINT",EDGE,{"derivedFrom":sQuery(id+"F8.wireOp",EDGE,"E23")}),-1.0]])]});
            var Q2;
            Q2=makeQuery(id+"F8.imprint","IMPRINT",FACE,{"disambiguationData":[TD([[makeQuery(id+"F8.imprint","IMPRINT",EDGE,{"derivedFrom":sQuery(id+"F8.wireOp",EDGE,"E27")}),1.0]])]});
            var Q3;
            Q3=makeQuery(id+"F8.imprint","IMPRINT",FACE,{"disambiguationData":[TD([[makeQuery(id+"F8.imprint","IMPRINT",EDGE,{"derivedFrom":sQuery(id+"F8.wireOp",EDGE,"E31")}),-1.0]])]});
            extrude(context, id + "F9", {"entities" : qUnion([Q0, Q1, Q2, Q3]), "operationType" : NewBodyOperationType.REMOVE, "endBound" : BoundingType.THROUGH_ALL, "oppositeDirection" : true, "depth" : 25 * mm, "offsetDistance" : 25 * mm});
        }
        {
            var Q0;
            {var subQ0=sQuery(id+"F2.wireOp",EDGE,"E2.1.4.0");var subQ1=sQuery(id+"F2.wireOp",EDGE,"E2.0.4.0");Q0=makeQuery(id+"F9.boolean.opBoolean","MERGE",FACE,{"derivedFrom":[makeQuery(id+"F5.boolean.opBoolean","MERGE",FACE,{"derivedFrom":[makeQuery(id+"F3.boolean.opBoolean","COPY",FACE,{"derivedFrom":makeQuery(id+"F3.opExtrude","SWEPT_FACE",FACE,{"disambiguationData":[OSD([subQ1])]})}),makeQuery(id+"F5.opExtrude","SWEPT_FACE",FACE,{"disambiguationData":[OSD([subQ1])]})]}),makeQuery(id+"F5.boolean.opBoolean","MERGE",FACE,{"derivedFrom":[makeQuery(id+"F3.boolean.opBoolean","COPY",FACE,{"derivedFrom":makeQuery(id+"F3.opExtrude","SWEPT_FACE",FACE,{"disambiguationData":[OSD([subQ0])]})}),makeQuery(id+"F5.opExtrude","SWEPT_FACE",FACE,{"disambiguationData":[OSD([subQ0])]})]})],"fromTools":[makeQuery(id+"F9.opExtrude","SWEPT_FACE",FACE,{"disambiguationData":[OSD([sQuery(id+"F8.wireOp",EDGE,"E21")])]})]});}
            var sketch = newSketch(context, id + "F10", { "sketchPlane" : qUnion([Q0])});
            skLineSegment(sketch, "E35", {"start": v(-26.56, 17) * mm, "end": v(-35.9, 3) * mm});
            skLineSegment(sketch, "E36", {"start": v(-35.9, 3) * mm, "end": v(-26.1, 3) * mm});
            skLineSegment(sketch, "E37", {"start": v(-26.1, 3) * mm, "end": v(-26.1, 17) * mm});
            skLineSegment(sketch, "E38", {"start": v(-26.1, 17) * mm, "end": v(-26.56, 17) * mm});
            skLineSegment(sketch, "E39", {"start": v(-23.1, 17) * mm, "end": v(-23.1, 3) * mm});
            skLineSegment(sketch, "E40", {"start": v(-23.1, 3) * mm, "end": v(-13.3, 3) * mm});
            skLineSegment(sketch, "E41", {"start": v(-13.3, 3) * mm, "end": v(-22.64, 17) * mm});
            skLineSegment(sketch, "E42", {"start": v(-22.64, 17) * mm, "end": v(-23.1, 17) * mm});
            skLineSegment(sketch, "E43", {"start": v(22.64, 17) * mm, "end": v(13.3, 3) * mm});
            skLineSegment(sketch, "E44", {"start": v(13.3, 3) * mm, "end": v(23.1, 3) * mm});
            skLineSegment(sketch, "E45", {"start": v(23.1, 3) * mm, "end": v(23.1, 17) * mm});
            skLineSegment(sketch, "E46", {"start": v(23.1, 17) * mm, "end": v(22.64, 17) * mm});
            skLineSegment(sketch, "E47", {"start": v(26.1, 17) * mm, "end": v(26.1, 3) * mm});
            skLineSegment(sketch, "E48", {"start": v(26.1, 3) * mm, "end": v(35.9, 3) * mm});
            skLineSegment(sketch, "E49", {"start": v(35.9, 3) * mm, "end": v(26.56, 17) * mm});
            skLineSegment(sketch, "E50", {"start": v(26.56, 17) * mm, "end": v(26.1, 17) * mm});
            skSolve(sketch);
        }
        {
            var Q0;
            Q0=makeQuery(id+"F10.imprint","IMPRINT",FACE,{"disambiguationData":[TD([[makeQuery(id+"F10.imprint","IMPRINT",EDGE,{"derivedFrom":sQuery(id+"F10.wireOp",EDGE,"E35")}),1.0]])]});
            var Q1;
            Q1=makeQuery(id+"F10.imprint","IMPRINT",FACE,{"disambiguationData":[TD([[makeQuery(id+"F10.imprint","IMPRINT",EDGE,{"derivedFrom":sQuery(id+"F10.wireOp",EDGE,"E39")}),1.0]])]});
            var Q2;
            Q2=makeQuery(id+"F10.imprint","IMPRINT",FACE,{"disambiguationData":[TD([[makeQuery(id+"F10.imprint","IMPRINT",EDGE,{"derivedFrom":sQuery(id+"F10.wireOp",EDGE,"E43")}),1.0]])]});
            var Q3;
            Q3=makeQuery(id+"F10.imprint","IMPRINT",FACE,{"disambiguationData":[TD([[makeQuery(id+"F10.imprint","IMPRINT",EDGE,{"derivedFrom":sQuery(id+"F10.wireOp",EDGE,"E47")}),1.0]])]});
            extrude(context, id + "F11", {"entities" : qUnion([Q0, Q1, Q2, Q3]), "operationType" : NewBodyOperationType.REMOVE, "endBound" : BoundingType.THROUGH_ALL, "oppositeDirection" : true, "depth" : 25 * mm, "offsetDistance" : 25 * mm});
        }
    });
